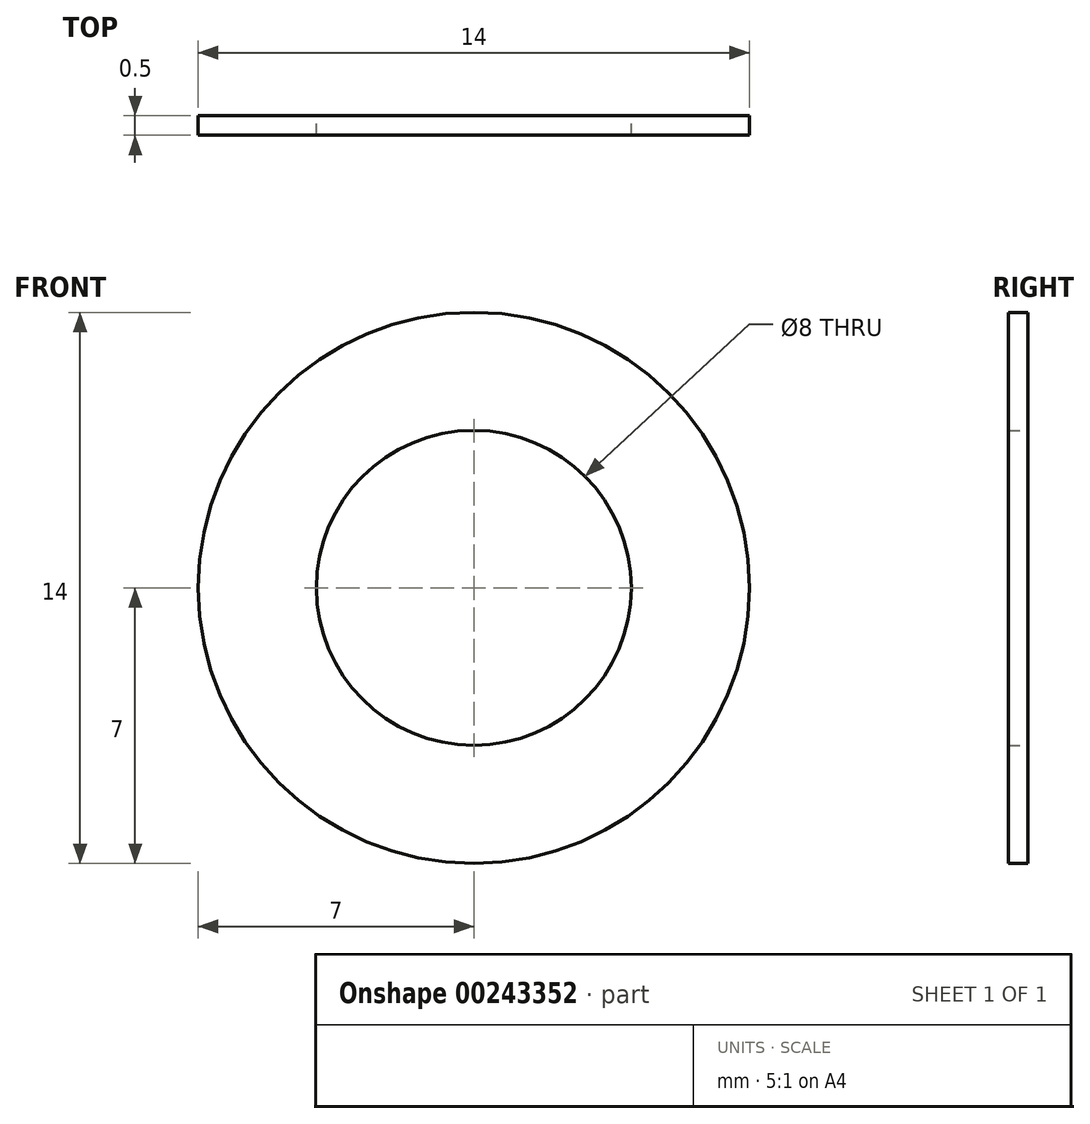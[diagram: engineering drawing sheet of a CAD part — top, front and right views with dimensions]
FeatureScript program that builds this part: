
annotation { "Feature Type Name" : "Feature", "Feature Type Description" : "" }
export const myFeature = defineFeature(function(context is Context, id is Id, definition is map)
    precondition{}
    {
        {
            var Q0;
            Q0=qCreatedBy(makeId("Front.planeOp"),FACE);
            var sketch = newSketch(context, id + "F0", { "sketchPlane" : qUnion([Q0])});
            skCircle(sketch, "E0", {"center": v(0, 0) * mm, "radius": 4 * mm});
            skCircle(sketch, "E1", {"center": v(0, 0) * mm, "radius": 7 * mm});
            skSolve(sketch);
        }
        {
            var Q0;
            Q0=makeQuery(id+"F0.imprint","IMPRINT",FACE,{"disambiguationData":[TD([[makeQuery(id+"F0.imprint","IMPRINT",EDGE,{"derivedFrom":sQuery(id+"F0.wireOp",EDGE,"E0")}),-1.0]])]});
            extrude(context, id + "F1", {"entities" : qUnion([Q0]), "depth" : .5 * mm});
        }
    });
